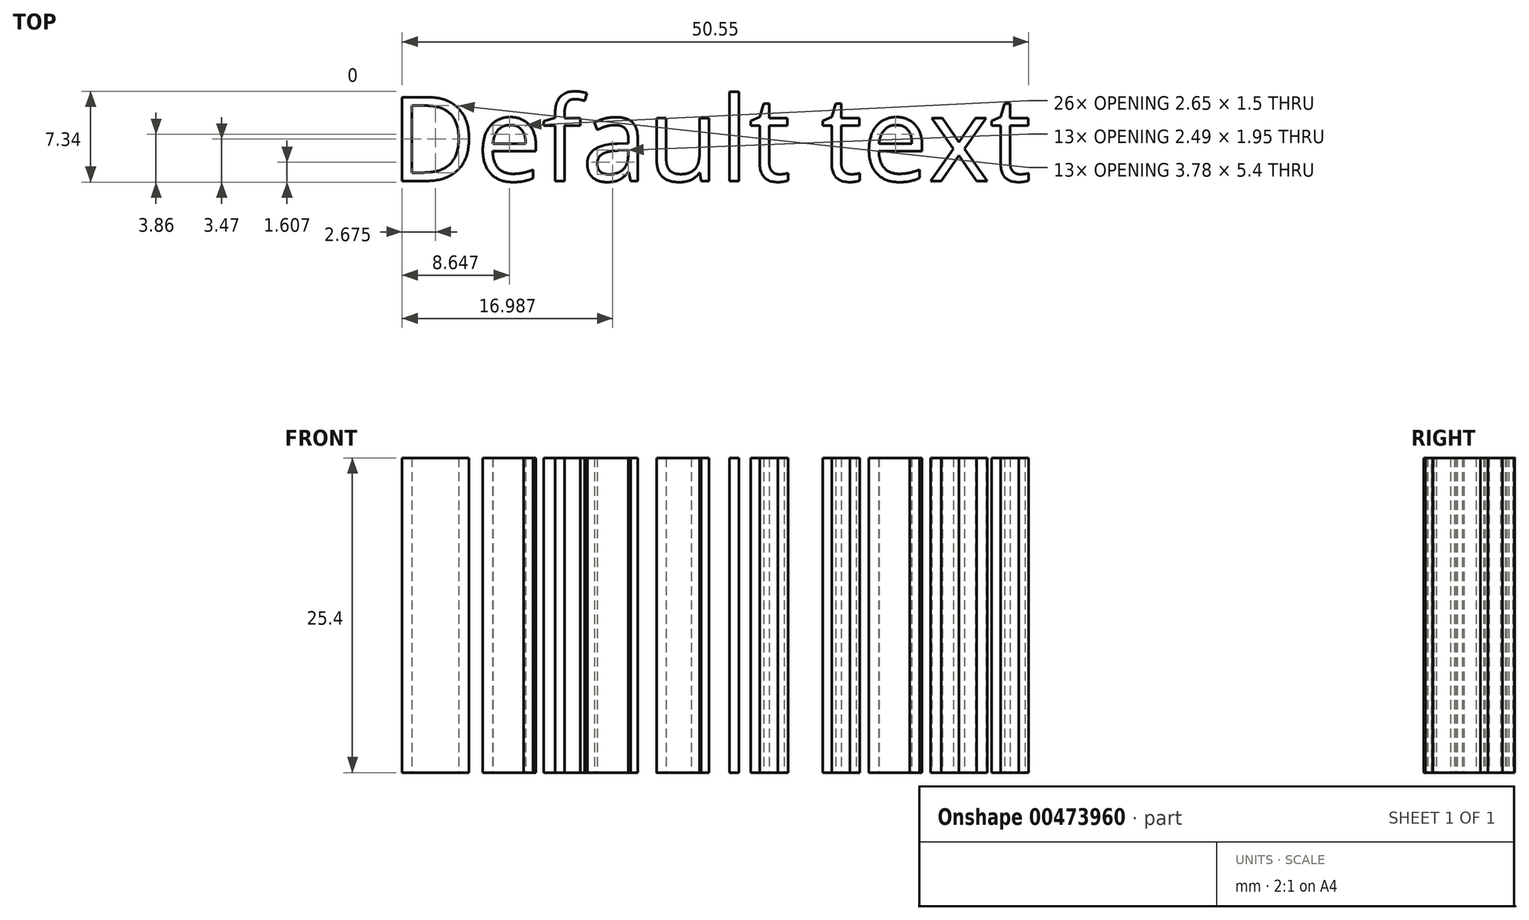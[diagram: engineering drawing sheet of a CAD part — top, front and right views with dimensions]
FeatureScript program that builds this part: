
annotation { "Feature Type Name" : "Feature", "Feature Type Description" : "" }
export const myFeature = defineFeature(function(context is Context, id is Id, definition is map)
    precondition{}
    {
        {
            var Q0;
            Q0=qCreatedBy(makeId("Top.planeOp"),FACE);
            var sketch = newSketch(context, id + "F0", { "sketchPlane" : qUnion([Q0])});
            skText(sketch, "E0", { "text": "Default text", "fontName": "OpenSans-Regular.ttf"});
            const initialGuessF0  = {"E0": [0, -0.00682, 1, 0, 0.00682]};
            skSetInitialGuess(sketch, initialGuessF0);
            skSolve(sketch);
        }
        {
            var Q0;
            Q0 = qSketchRegion(id + "F0", true);
            extrude(context, id + "F1", {"entities" : qUnion([Q0]), "depth" : 25.4 * mm});
        }
    });
